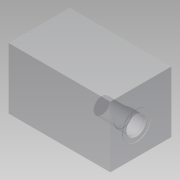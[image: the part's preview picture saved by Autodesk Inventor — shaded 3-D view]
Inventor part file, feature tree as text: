
AUTODESK INVENTOR PART (.ipt)
format: ipt  version: 2014 (Build 180170000, 170)  size: 160,256 bytes
history: native  units: mm
features: other x48, extrude x9, sketch x9
ambient origin geometry x8: Origin, YZ Plane, XZ Plane, XY Plane, X Axis, Y Axis, Z Axis, Center Point
bodies: 实体1 (feature_tree)
feature tree (66):
  extrude  "拉伸1"  Depth=41.28mm
  other  "UCS1"
  other  "UCS2"
  other  "UCS3"
  other  "UCS4"
  other  "UCS5"
  other  "UCS6"
  extrude  "拉伸2"  Depth=39.0mm
  extrude  "拉伸3"  Depth=50.8mm
  extrude  "拉伸4"  Depth=50.8mm
  extrude  "拉伸5"  Depth=5.0mm
  extrude  "拉伸6"  Depth=50.8mm
  extrude  "拉伸7"  Depth=50.8mm TaperAngle=0.0deg
  extrude  "拉伸9"  Depth=50.8mm
  extrude  "拉伸11"  Depth=50.8mm
  sketch  "草图1"  dims[d0=90.0mm d1=0.0mm]
  sketch  "草图2"  dims[d2=0.0mm d3=0.0mm d4=0.0mm d5=0.0mm d6=0.0mm d7=0.0mm]
  sketch  "草图3"  dims[d8=0.0mm d9=0.0mm d10=0.0mm d11=0.0mm d12=0.0mm d13=0.0mm]
  sketch  "草图4"  dims[d14=0.0mm d15=0.0mm d16=0.0mm d17=0.0mm d18=0.0mm d19=0.0mm]
  sketch  "草图5"  dims[d20=0.0mm d21=0.0mm d22=0.0mm d23=0.0mm d24=0.0mm d25=0.0mm]
  sketch  "草图6"  dims[d26=0.0mm d27=0.0mm d28=0.0mm d29=0.0mm d30=0.0mm d31=0.0mm]
  sketch  "草图7"  dims[d32=0.0mm d33=0.0mm d34=0.0mm d35=0.0mm d36=0.0mm d37=0.0mm d38=41.28mm]
  sketch  "草图9"  dims[d39=40.0mm d40=39.0mm]
  sketch  "草图12"  dims[d41=0.79mm d42=0.0mm d43=29.16mm d44=3.3mm d45=-2.617994mm d46=5.0mm d47=-7.853982mm d48=26.99mm d49=19.05mm d50=0.0mm d51=3.0mm d52=-10.471976mm d53=24.69mm d54=23.01mm d55=0.0mm d59=50.8mm d60=-10.471976mm d64=24.0mm d65=50.8mm d66=0.0mm]
  other  "UCS1: YZ 平面"
  other  "UCS1: XZ 平面"
  other  "UCS1: XY 平面"
  other  "UCS1: X 轴"
  other  "UCS1: Y 轴"
  other  "UCS1: Z 轴"
  other  "UCS1: 原点"
  other  "UCS2: YZ 平面"
  other  "UCS2: XZ 平面"
  other  "UCS2: XY 平面"
  other  "UCS2: X 轴"
  other  "UCS2: Y 轴"
  other  "UCS2: Z 轴"
  other  "UCS2: 原点"
  other  "UCS3: YZ 平面"
  other  "UCS3: XZ 平面"
  other  "UCS3: XY 平面"
  other  "UCS3: X 轴"
  other  "UCS3: Y 轴"
  other  "UCS3: Z 轴"
  other  "UCS3: 原点"
  other  "UCS4: YZ 平面"
  other  "UCS4: XZ 平面"
  other  "UCS4: XY 平面"
  other  "UCS4: X 轴"
  other  "UCS4: Y 轴"
  other  "UCS4: Z 轴"
  other  "UCS4: 原点"
  other  "UCS5: YZ 平面"
  other  "UCS5: XZ 平面"
  other  "UCS5: XY 平面"
  other  "UCS5: X 轴"
  other  "UCS5: Y 轴"
  other  "UCS5: Z 轴"
  other  "UCS5: 原点"
  other  "UCS6: YZ 平面"
  other  "UCS6: XZ 平面"
  other  "UCS6: XY 平面"
  other  "UCS6: X 轴"
  other  "UCS6: Y 轴"
  other  "UCS6: Z 轴"
  other  "UCS6: 原点"
